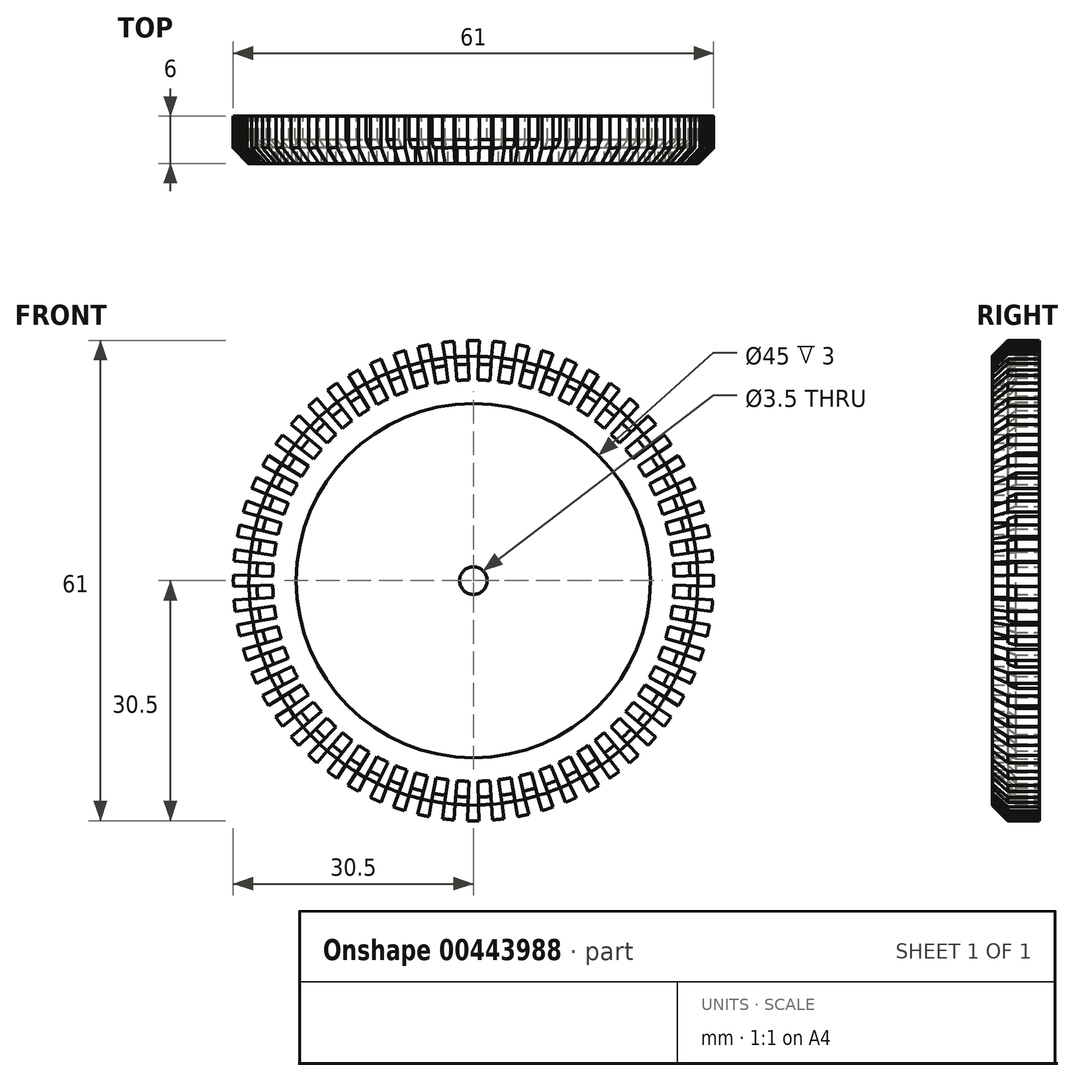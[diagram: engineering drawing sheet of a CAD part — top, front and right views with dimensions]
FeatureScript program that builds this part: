
annotation { "Feature Type Name" : "Feature", "Feature Type Description" : "" }
export const myFeature = defineFeature(function(context is Context, id is Id, definition is map)
    precondition{}
    {
        {
            var Q0;
            Q0=qCreatedBy(makeId("Front.planeOp"),FACE);
            var sketch = newSketch(context, id + "F0", { "sketchPlane" : qUnion([Q0])});
            skCircle(sketch, "E0", {"center": v(0, 0) * mm, "radius": 30.5 * mm});
            skLineSegment(sketch, "E1", {"start": v(0, 0) * mm, "end": v(-1.6, 30.46) * mm});
            skLineSegment(sketch, "E2", {"start": v(0, 0) * mm, "end": v(1.6, 30.46) * mm});
            skCircle(sketch, "E3", {"center": v(0, 0) * mm, "radius": 28.5 * mm});
            skCircle(sketch, "E4", {"center": v(0, 0) * mm, "radius": 25.5 * mm});
            skCircle(sketch, "E5", {"center": v(0, 0) * mm, "radius": 22.5 * mm});
            skLineSegment(sketch, "E6", {"start": v(-1.6, 30.46) * mm, "end": v(1.6, 30.46) * mm, "construction": true});
            skLineSegment(sketch, "E7", {"start": v(0, 0) * mm, "end": v(0, 30.5) * mm, "construction": true});
            skPoint(sketch, "E7.endSnap0", {"position": v(0, 30.46) * mm});
            skLineSegment(sketch, "E8", {"start": v(-1.33, 25.47) * mm, "end": v(1.33, 25.47) * mm, "construction": true});
            skLineSegment(sketch, "E9", {"start": v(-0.55, 25.5) * mm, "end": v(-0.75, 31.15) * mm});
            skLineSegment(sketch, "E10", {"start": v(0.55, 25.5) * mm, "end": v(0.75, 30.5) * mm});
            skCircle(sketch, "E11", {"center": v(0, 0) * mm, "radius": 1.75 * mm});
            skSolve(sketch);
        }
        {
            var Q0;
            {var subQ5=sQuery(id+"F0.wireOp",EDGE,"E5");var subQ6=sQuery(id+"F0.wireOp",EDGE,"E1");var subQ7=makeQuery(id+"F0.imprint","INTERSECT",VERTEX,{"derivedFrom":[subQ6,subQ5]});Q0=makeQuery(id+"F0.imprint","IMPRINT",FACE,{"disambiguationData":[TD([[makeQuery(id+"F0.imprint","IMPRINT",EDGE,{"disambiguationData":[TD([[subQ7,-1.0]])],"derivedFrom":subQ6}),-1.0]])]});}
            var Q1;
            {var subQ0=sQuery(id+"F0.wireOp",EDGE,"E10");var subQ1=sQuery(id+"F0.wireOp",EDGE,"E3");var subQ2=makeQuery(id+"F0.imprint","INTERSECT",VERTEX,{"derivedFrom":[subQ1,subQ0]});Q1=makeQuery(id+"F0.imprint","IMPRINT",FACE,{"disambiguationData":[TD([[makeQuery(id+"F0.imprint","IMPRINT",EDGE,{"disambiguationData":[TD([[subQ2,-1.0]])],"derivedFrom":subQ1}),1.0]])]});}
            var Q2;
            {var subQ0=sQuery(id+"F0.wireOp",EDGE,"E10");var subQ1=sQuery(id+"F0.wireOp",EDGE,"E0");var subQ2=makeQuery(id+"F0.imprint","INTERSECT",VERTEX,{"derivedFrom":[subQ1,subQ0]});Q2=makeQuery(id+"F0.imprint","IMPRINT",FACE,{"disambiguationData":[TD([[makeQuery(id+"F0.imprint","IMPRINT",EDGE,{"disambiguationData":[TD([[subQ2,-1.0]])],"derivedFrom":subQ1}),1.0]])]});}
            extrude(context, id + "F1", {"entities" : qUnion([Q0, Q1, Q2]), "depth" : 6 * mm});
        }
        {
            var Q0;
            Q0=makeQuery(id+"F1.opExtrude","SWEPT_FACE",FACE,{"disambiguationData":[OSD([sQuery(id+"F0.wireOp",EDGE,"E10")])]});
            var sketch = newSketch(context, id + "F2", { "sketchPlane" : qUnion([Q0])});
            skLineSegment(sketch, "E12.0", {"start": v(0, 25.5) * mm, "end": v(0, 30.5) * mm});
            skLineSegment(sketch, "E12.1", {"start": v(-6, 30.5) * mm, "end": v(0, 30.5) * mm});
            skLineSegment(sketch, "E12.2", {"start": v(-6, 25.5) * mm, "end": v(-6, 30.5) * mm});
            skLineSegment(sketch, "E12.3", {"start": v(-6, 25.5) * mm, "end": v(0, 25.5) * mm});
            skLineSegment(sketch, "E13", {"start": v(-6, 28.5) * mm, "end": v(0, 28.5) * mm, "construction": true});
            skLineSegment(sketch, "E14", {"start": v(-4, 25.5) * mm, "end": v(-4, 30.5) * mm, "construction": true});
            skLineSegment(sketch, "E15", {"start": v(-6, 28.5) * mm, "end": v(-4, 30.5) * mm});
            skSolve(sketch);
        }
        {
            var Q0;
            {var subQ3=sQuery(id+"F2.wireOp",EDGE,"E15");Q0=makeQuery(id+"F2.imprint","IMPRINT",FACE,{"disambiguationData":[TD([[makeQuery(id+"F2.imprint","IMPRINT",EDGE,{"derivedFrom":subQ3}),1.0]])]});}
            extrude(context, id + "F3", {"entities" : qUnion([Q0]), "operationType" : NewBodyOperationType.REMOVE, "endBound" : BoundingType.THROUGH_ALL, "oppositeDirection" : true, "depth" : 25 * mm});
        }
        {
            var Q0;
            Q0=makeQuery(id+"F1.opExtrude","SWEPT_BODY",BODY,{"disambiguationData":[OSD([sQuery(id+"F0.wireOp",EDGE,"E0"),sQuery(id+"F0.wireOp",EDGE,"E1"),sQuery(id+"F0.wireOp",EDGE,"E2"),sQuery(id+"F0.wireOp",EDGE,"E4"),sQuery(id+"F0.wireOp",EDGE,"E5"),sQuery(id+"F0.wireOp",EDGE,"E9"),sQuery(id+"F0.wireOp",EDGE,"E10")])]});
            var Q1;
            Q1=sQuery(id+"F0.wireOp",EDGE,"E5");
            circularPattern(context, id + "F4", {"operationType" : NewBodyOperationType.ADD, "entities" : qUnion([Q0]), "axis" : qUnion([Q1]), "angle" : 360 * degree, "instanceCount" : 60, "equalSpace" : true});
        }
        {
            var Q0;
            {var subQ0=sQuery(id+"F0.wireOp",EDGE,"E11");var subQ1=sQuery(id+"F0.wireOp",EDGE,"E1");var subQ2=makeQuery(id+"F0.imprint","INTERSECT",VERTEX,{"derivedFrom":[subQ1,subQ0]});Q0=makeQuery(id+"F0.imprint","IMPRINT",FACE,{"disambiguationData":[TD([[makeQuery(id+"F0.imprint","IMPRINT",EDGE,{"disambiguationData":[TD([[subQ2,-1.0]])],"derivedFrom":subQ1}),1.0]])]});}
            var Q1;
            {var subQ0=sQuery(id+"F0.wireOp",EDGE,"E11");var subQ1=sQuery(id+"F0.wireOp",EDGE,"E1");var subQ2=makeQuery(id+"F0.imprint","INTERSECT",VERTEX,{"derivedFrom":[subQ1,subQ0]});Q1=makeQuery(id+"F0.imprint","IMPRINT",FACE,{"disambiguationData":[TD([[makeQuery(id+"F0.imprint","IMPRINT",EDGE,{"disambiguationData":[TD([[subQ2,-1.0]])],"derivedFrom":subQ1}),-1.0]])]});}
            extrude(context, id + "F5", {"entities" : qUnion([Q0, Q1]), "operationType" : NewBodyOperationType.ADD, "depth" : 3 * mm});
        }
        {
            var Q0;
            {var subQ0=sQuery(id+"F0.wireOp",EDGE,"E4");var subQ1=sQuery(id+"F0.wireOp",EDGE,"E1");var subQ2=makeQuery(id+"F0.imprint","INTERSECT",VERTEX,{"derivedFrom":[subQ1,subQ0]});Q0=makeQuery(id+"F0.imprint","IMPRINT",FACE,{"disambiguationData":[TD([[makeQuery(id+"F0.imprint","IMPRINT",EDGE,{"disambiguationData":[TD([[subQ2,-1.0]])],"derivedFrom":subQ1}),1.0]])]});}
            var Q1;
            {var subQ0=sQuery(id+"F0.wireOp",EDGE,"E4");var subQ1=sQuery(id+"F0.wireOp",EDGE,"E2");var subQ2=makeQuery(id+"F0.imprint","INTERSECT",VERTEX,{"derivedFrom":[subQ1,subQ0]});Q1=makeQuery(id+"F0.imprint","IMPRINT",FACE,{"disambiguationData":[TD([[makeQuery(id+"F0.imprint","IMPRINT",EDGE,{"disambiguationData":[TD([[subQ2,-1.0]])],"derivedFrom":subQ1}),1.0]])]});}
            var Q2;
            {var subQ0=sQuery(id+"F0.wireOp",EDGE,"E4");var subQ1=sQuery(id+"F0.wireOp",EDGE,"E1");var subQ2=makeQuery(id+"F0.imprint","INTERSECT",VERTEX,{"derivedFrom":[subQ1,subQ0]});Q2=makeQuery(id+"F0.imprint","IMPRINT",FACE,{"disambiguationData":[TD([[makeQuery(id+"F0.imprint","IMPRINT",EDGE,{"disambiguationData":[TD([[subQ2,-1.0]])],"derivedFrom":subQ1}),-1.0]])]});}
            extrude(context, id + "F6", {"entities" : qUnion([Q0, Q1, Q2]), "operationType" : NewBodyOperationType.ADD, "depth" : 4 * mm});
        }
        {
            var Q0;
            {var subQ0=sQuery(id+"F0.wireOp",EDGE,"E9");var subQ1=sQuery(id+"F0.wireOp",EDGE,"E3");Q0=makeQuery(id+"F6.boolean.opBoolean","SPLIT",EDGE,{"disambiguationData":[TD([makeQuery(id+"F4.opPattern","COPY",FACE,{"derivedFrom":makeQuery(id+"F1.opExtrude","SWEPT_FACE",FACE,{"disambiguationData":[OSD([subQ0])]}),"instanceName":"56"})])],"derivedFrom":makeQuery(id+"F6.opExtrude","CAP_EDGE",EDGE,{"disambiguationData":[OSD([subQ1])],"isStart":false})});}
            var Q1;
            {var subQ0=sQuery(id+"F0.wireOp",EDGE,"E9");var subQ2=sQuery(id+"F0.wireOp",EDGE,"E3");Q1=makeQuery(id+"F6.boolean.opBoolean","SPLIT",EDGE,{"disambiguationData":[TD([makeQuery(id+"F4.opPattern","COPY",FACE,{"derivedFrom":makeQuery(id+"F1.opExtrude","SWEPT_FACE",FACE,{"disambiguationData":[OSD([subQ0])]}),"instanceName":"55"})])],"derivedFrom":makeQuery(id+"F6.opExtrude","CAP_EDGE",EDGE,{"disambiguationData":[OSD([subQ2])],"isStart":false})});}
            var Q2;
            {var subQ0=sQuery(id+"F0.wireOp",EDGE,"E9");var subQ2=sQuery(id+"F0.wireOp",EDGE,"E3");Q2=makeQuery(id+"F6.boolean.opBoolean","SPLIT",EDGE,{"disambiguationData":[TD([makeQuery(id+"F4.opPattern","COPY",FACE,{"derivedFrom":makeQuery(id+"F1.opExtrude","SWEPT_FACE",FACE,{"disambiguationData":[OSD([subQ0])]}),"instanceName":"54"})])],"derivedFrom":makeQuery(id+"F6.opExtrude","CAP_EDGE",EDGE,{"disambiguationData":[OSD([subQ2])],"isStart":false})});}
            var Q3;
            {var subQ0=sQuery(id+"F0.wireOp",EDGE,"E9");var subQ2=sQuery(id+"F0.wireOp",EDGE,"E3");Q3=makeQuery(id+"F6.boolean.opBoolean","SPLIT",EDGE,{"disambiguationData":[TD([makeQuery(id+"F4.opPattern","COPY",FACE,{"derivedFrom":makeQuery(id+"F1.opExtrude","SWEPT_FACE",FACE,{"disambiguationData":[OSD([subQ0])]}),"instanceName":"57"})])],"derivedFrom":makeQuery(id+"F6.opExtrude","CAP_EDGE",EDGE,{"disambiguationData":[OSD([subQ2])],"isStart":false})});}
            var Q4;
            {var subQ0=sQuery(id+"F0.wireOp",EDGE,"E9");var subQ2=sQuery(id+"F0.wireOp",EDGE,"E3");Q4=makeQuery(id+"F6.boolean.opBoolean","SPLIT",EDGE,{"disambiguationData":[TD([makeQuery(id+"F4.opPattern","COPY",FACE,{"derivedFrom":makeQuery(id+"F1.opExtrude","SWEPT_FACE",FACE,{"disambiguationData":[OSD([subQ0])]}),"instanceName":"58"})])],"derivedFrom":makeQuery(id+"F6.opExtrude","CAP_EDGE",EDGE,{"disambiguationData":[OSD([subQ2])],"isStart":false})});}
            var Q5;
            {var subQ0=sQuery(id+"F0.wireOp",EDGE,"E10");var subQ1=sQuery(id+"F0.wireOp",EDGE,"E3");Q5=makeQuery(id+"F6.boolean.opBoolean","SPLIT",EDGE,{"disambiguationData":[TD([makeQuery(id+"F1.opExtrude","SWEPT_FACE",FACE,{"disambiguationData":[OSD([subQ0])]})])],"derivedFrom":makeQuery(id+"F6.opExtrude","CAP_EDGE",EDGE,{"disambiguationData":[OSD([subQ1])],"isStart":false})});}
            var Q6;
            {var subQ0=sQuery(id+"F0.wireOp",EDGE,"E9");var subQ2=sQuery(id+"F0.wireOp",EDGE,"E3");Q6=makeQuery(id+"F6.boolean.opBoolean","SPLIT",EDGE,{"disambiguationData":[TD([makeQuery(id+"F1.opExtrude","SWEPT_FACE",FACE,{"disambiguationData":[OSD([subQ0])]})])],"derivedFrom":makeQuery(id+"F6.opExtrude","CAP_EDGE",EDGE,{"disambiguationData":[OSD([subQ2])],"isStart":false})});}
            var Q7;
            {var subQ0=sQuery(id+"F0.wireOp",EDGE,"E9");var subQ1=sQuery(id+"F0.wireOp",EDGE,"E3");Q7=makeQuery(id+"F6.boolean.opBoolean","SPLIT",EDGE,{"disambiguationData":[TD([makeQuery(id+"F4.opPattern","COPY",FACE,{"derivedFrom":makeQuery(id+"F1.opExtrude","SWEPT_FACE",FACE,{"disambiguationData":[OSD([subQ0])]}),"instanceName":"1"})])],"derivedFrom":makeQuery(id+"F6.opExtrude","CAP_EDGE",EDGE,{"disambiguationData":[OSD([subQ1])],"isStart":false})});}
            var Q8;
            {var subQ0=sQuery(id+"F0.wireOp",EDGE,"E9");var subQ2=sQuery(id+"F0.wireOp",EDGE,"E3");Q8=makeQuery(id+"F6.boolean.opBoolean","SPLIT",EDGE,{"disambiguationData":[TD([makeQuery(id+"F4.opPattern","COPY",FACE,{"derivedFrom":makeQuery(id+"F1.opExtrude","SWEPT_FACE",FACE,{"disambiguationData":[OSD([subQ0])]}),"instanceName":"2"})])],"derivedFrom":makeQuery(id+"F6.opExtrude","CAP_EDGE",EDGE,{"disambiguationData":[OSD([subQ2])],"isStart":false})});}
            var Q9;
            {var subQ0=sQuery(id+"F0.wireOp",EDGE,"E9");var subQ2=sQuery(id+"F0.wireOp",EDGE,"E3");Q9=makeQuery(id+"F6.boolean.opBoolean","SPLIT",EDGE,{"disambiguationData":[TD([makeQuery(id+"F4.opPattern","COPY",FACE,{"derivedFrom":makeQuery(id+"F1.opExtrude","SWEPT_FACE",FACE,{"disambiguationData":[OSD([subQ0])]}),"instanceName":"53"})])],"derivedFrom":makeQuery(id+"F6.opExtrude","CAP_EDGE",EDGE,{"disambiguationData":[OSD([subQ2])],"isStart":false})});}
            var Q10;
            {var subQ0=sQuery(id+"F0.wireOp",EDGE,"E9");var subQ2=sQuery(id+"F0.wireOp",EDGE,"E3");Q10=makeQuery(id+"F6.boolean.opBoolean","SPLIT",EDGE,{"disambiguationData":[TD([makeQuery(id+"F4.opPattern","COPY",FACE,{"derivedFrom":makeQuery(id+"F1.opExtrude","SWEPT_FACE",FACE,{"disambiguationData":[OSD([subQ0])]}),"instanceName":"52"})])],"derivedFrom":makeQuery(id+"F6.opExtrude","CAP_EDGE",EDGE,{"disambiguationData":[OSD([subQ2])],"isStart":false})});}
            var Q11;
            {var subQ0=sQuery(id+"F0.wireOp",EDGE,"E9");var subQ1=sQuery(id+"F0.wireOp",EDGE,"E3");Q11=makeQuery(id+"F6.boolean.opBoolean","SPLIT",EDGE,{"disambiguationData":[TD([makeQuery(id+"F4.opPattern","COPY",FACE,{"derivedFrom":makeQuery(id+"F1.opExtrude","SWEPT_FACE",FACE,{"disambiguationData":[OSD([subQ0])]}),"instanceName":"51"})])],"derivedFrom":makeQuery(id+"F6.opExtrude","CAP_EDGE",EDGE,{"disambiguationData":[OSD([subQ1])],"isStart":false})});}
            var Q12;
            {var subQ0=sQuery(id+"F0.wireOp",EDGE,"E9");var subQ2=sQuery(id+"F0.wireOp",EDGE,"E3");Q12=makeQuery(id+"F6.boolean.opBoolean","SPLIT",EDGE,{"disambiguationData":[TD([makeQuery(id+"F4.opPattern","COPY",FACE,{"derivedFrom":makeQuery(id+"F1.opExtrude","SWEPT_FACE",FACE,{"disambiguationData":[OSD([subQ0])]}),"instanceName":"50"})])],"derivedFrom":makeQuery(id+"F6.opExtrude","CAP_EDGE",EDGE,{"disambiguationData":[OSD([subQ2])],"isStart":false})});}
            var Q13;
            {var subQ0=sQuery(id+"F0.wireOp",EDGE,"E9");var subQ2=sQuery(id+"F0.wireOp",EDGE,"E3");Q13=makeQuery(id+"F6.boolean.opBoolean","SPLIT",EDGE,{"disambiguationData":[TD([makeQuery(id+"F4.opPattern","COPY",FACE,{"derivedFrom":makeQuery(id+"F1.opExtrude","SWEPT_FACE",FACE,{"disambiguationData":[OSD([subQ0])]}),"instanceName":"49"})])],"derivedFrom":makeQuery(id+"F6.opExtrude","CAP_EDGE",EDGE,{"disambiguationData":[OSD([subQ2])],"isStart":false})});}
            var Q14;
            {var subQ0=sQuery(id+"F0.wireOp",EDGE,"E9");var subQ2=sQuery(id+"F0.wireOp",EDGE,"E3");Q14=makeQuery(id+"F6.boolean.opBoolean","SPLIT",EDGE,{"disambiguationData":[TD([makeQuery(id+"F4.opPattern","COPY",FACE,{"derivedFrom":makeQuery(id+"F1.opExtrude","SWEPT_FACE",FACE,{"disambiguationData":[OSD([subQ0])]}),"instanceName":"48"})])],"derivedFrom":makeQuery(id+"F6.opExtrude","CAP_EDGE",EDGE,{"disambiguationData":[OSD([subQ2])],"isStart":false})});}
            var Q15;
            {var subQ0=sQuery(id+"F0.wireOp",EDGE,"E9");var subQ2=sQuery(id+"F0.wireOp",EDGE,"E3");Q15=makeQuery(id+"F6.boolean.opBoolean","SPLIT",EDGE,{"disambiguationData":[TD([makeQuery(id+"F4.opPattern","COPY",FACE,{"derivedFrom":makeQuery(id+"F1.opExtrude","SWEPT_FACE",FACE,{"disambiguationData":[OSD([subQ0])]}),"instanceName":"47"})])],"derivedFrom":makeQuery(id+"F6.opExtrude","CAP_EDGE",EDGE,{"disambiguationData":[OSD([subQ2])],"isStart":false})});}
            var Q16;
            {var subQ0=sQuery(id+"F0.wireOp",EDGE,"E9");var subQ1=sQuery(id+"F0.wireOp",EDGE,"E3");Q16=makeQuery(id+"F6.boolean.opBoolean","SPLIT",EDGE,{"disambiguationData":[TD([makeQuery(id+"F4.opPattern","COPY",FACE,{"derivedFrom":makeQuery(id+"F1.opExtrude","SWEPT_FACE",FACE,{"disambiguationData":[OSD([subQ0])]}),"instanceName":"46"})])],"derivedFrom":makeQuery(id+"F6.opExtrude","CAP_EDGE",EDGE,{"disambiguationData":[OSD([subQ1])],"isStart":false})});}
            var Q17;
            {var subQ0=sQuery(id+"F0.wireOp",EDGE,"E9");var subQ2=sQuery(id+"F0.wireOp",EDGE,"E3");Q17=makeQuery(id+"F6.boolean.opBoolean","SPLIT",EDGE,{"disambiguationData":[TD([makeQuery(id+"F4.opPattern","COPY",FACE,{"derivedFrom":makeQuery(id+"F1.opExtrude","SWEPT_FACE",FACE,{"disambiguationData":[OSD([subQ0])]}),"instanceName":"45"})])],"derivedFrom":makeQuery(id+"F6.opExtrude","CAP_EDGE",EDGE,{"disambiguationData":[OSD([subQ2])],"isStart":false})});}
            var Q18;
            {var subQ0=sQuery(id+"F0.wireOp",EDGE,"E9");var subQ2=sQuery(id+"F0.wireOp",EDGE,"E3");Q18=makeQuery(id+"F6.boolean.opBoolean","SPLIT",EDGE,{"disambiguationData":[TD([makeQuery(id+"F4.opPattern","COPY",FACE,{"derivedFrom":makeQuery(id+"F1.opExtrude","SWEPT_FACE",FACE,{"disambiguationData":[OSD([subQ0])]}),"instanceName":"44"})])],"derivedFrom":makeQuery(id+"F6.opExtrude","CAP_EDGE",EDGE,{"disambiguationData":[OSD([subQ2])],"isStart":false})});}
            var Q19;
            {var subQ0=sQuery(id+"F0.wireOp",EDGE,"E9");var subQ2=sQuery(id+"F0.wireOp",EDGE,"E3");Q19=makeQuery(id+"F6.boolean.opBoolean","SPLIT",EDGE,{"disambiguationData":[TD([makeQuery(id+"F4.opPattern","COPY",FACE,{"derivedFrom":makeQuery(id+"F1.opExtrude","SWEPT_FACE",FACE,{"disambiguationData":[OSD([subQ0])]}),"instanceName":"43"})])],"derivedFrom":makeQuery(id+"F6.opExtrude","CAP_EDGE",EDGE,{"disambiguationData":[OSD([subQ2])],"isStart":false})});}
            var Q20;
            {var subQ0=sQuery(id+"F0.wireOp",EDGE,"E9");var subQ2=sQuery(id+"F0.wireOp",EDGE,"E3");Q20=makeQuery(id+"F6.boolean.opBoolean","SPLIT",EDGE,{"disambiguationData":[TD([makeQuery(id+"F4.opPattern","COPY",FACE,{"derivedFrom":makeQuery(id+"F1.opExtrude","SWEPT_FACE",FACE,{"disambiguationData":[OSD([subQ0])]}),"instanceName":"42"})])],"derivedFrom":makeQuery(id+"F6.opExtrude","CAP_EDGE",EDGE,{"disambiguationData":[OSD([subQ2])],"isStart":false})});}
            var Q21;
            {var subQ0=sQuery(id+"F0.wireOp",EDGE,"E9");var subQ1=sQuery(id+"F0.wireOp",EDGE,"E3");Q21=makeQuery(id+"F6.boolean.opBoolean","SPLIT",EDGE,{"disambiguationData":[TD([makeQuery(id+"F4.opPattern","COPY",FACE,{"derivedFrom":makeQuery(id+"F1.opExtrude","SWEPT_FACE",FACE,{"disambiguationData":[OSD([subQ0])]}),"instanceName":"41"})])],"derivedFrom":makeQuery(id+"F6.opExtrude","CAP_EDGE",EDGE,{"disambiguationData":[OSD([subQ1])],"isStart":false})});}
            var Q22;
            {var subQ0=sQuery(id+"F0.wireOp",EDGE,"E9");var subQ2=sQuery(id+"F0.wireOp",EDGE,"E3");Q22=makeQuery(id+"F6.boolean.opBoolean","SPLIT",EDGE,{"disambiguationData":[TD([makeQuery(id+"F4.opPattern","COPY",FACE,{"derivedFrom":makeQuery(id+"F1.opExtrude","SWEPT_FACE",FACE,{"disambiguationData":[OSD([subQ0])]}),"instanceName":"40"})])],"derivedFrom":makeQuery(id+"F6.opExtrude","CAP_EDGE",EDGE,{"disambiguationData":[OSD([subQ2])],"isStart":false})});}
            var Q23;
            {var subQ0=sQuery(id+"F0.wireOp",EDGE,"E9");var subQ2=sQuery(id+"F0.wireOp",EDGE,"E3");Q23=makeQuery(id+"F6.boolean.opBoolean","SPLIT",EDGE,{"disambiguationData":[TD([makeQuery(id+"F4.opPattern","COPY",FACE,{"derivedFrom":makeQuery(id+"F1.opExtrude","SWEPT_FACE",FACE,{"disambiguationData":[OSD([subQ0])]}),"instanceName":"39"})])],"derivedFrom":makeQuery(id+"F6.opExtrude","CAP_EDGE",EDGE,{"disambiguationData":[OSD([subQ2])],"isStart":false})});}
            var Q24;
            {var subQ0=sQuery(id+"F0.wireOp",EDGE,"E9");var subQ2=sQuery(id+"F0.wireOp",EDGE,"E3");Q24=makeQuery(id+"F6.boolean.opBoolean","SPLIT",EDGE,{"disambiguationData":[TD([makeQuery(id+"F4.opPattern","COPY",FACE,{"derivedFrom":makeQuery(id+"F1.opExtrude","SWEPT_FACE",FACE,{"disambiguationData":[OSD([subQ0])]}),"instanceName":"38"})])],"derivedFrom":makeQuery(id+"F6.opExtrude","CAP_EDGE",EDGE,{"disambiguationData":[OSD([subQ2])],"isStart":false})});}
            var Q25;
            {var subQ0=sQuery(id+"F0.wireOp",EDGE,"E9");var subQ2=sQuery(id+"F0.wireOp",EDGE,"E3");Q25=makeQuery(id+"F6.boolean.opBoolean","SPLIT",EDGE,{"disambiguationData":[TD([makeQuery(id+"F4.opPattern","COPY",FACE,{"derivedFrom":makeQuery(id+"F1.opExtrude","SWEPT_FACE",FACE,{"disambiguationData":[OSD([subQ0])]}),"instanceName":"37"})])],"derivedFrom":makeQuery(id+"F6.opExtrude","CAP_EDGE",EDGE,{"disambiguationData":[OSD([subQ2])],"isStart":false})});}
            var Q26;
            {var subQ0=sQuery(id+"F0.wireOp",EDGE,"E9");var subQ1=sQuery(id+"F0.wireOp",EDGE,"E3");Q26=makeQuery(id+"F6.boolean.opBoolean","SPLIT",EDGE,{"disambiguationData":[TD([makeQuery(id+"F4.opPattern","COPY",FACE,{"derivedFrom":makeQuery(id+"F1.opExtrude","SWEPT_FACE",FACE,{"disambiguationData":[OSD([subQ0])]}),"instanceName":"36"})])],"derivedFrom":makeQuery(id+"F6.opExtrude","CAP_EDGE",EDGE,{"disambiguationData":[OSD([subQ1])],"isStart":false})});}
            var Q27;
            {var subQ0=sQuery(id+"F0.wireOp",EDGE,"E9");var subQ2=sQuery(id+"F0.wireOp",EDGE,"E3");Q27=makeQuery(id+"F6.boolean.opBoolean","SPLIT",EDGE,{"disambiguationData":[TD([makeQuery(id+"F4.opPattern","COPY",FACE,{"derivedFrom":makeQuery(id+"F1.opExtrude","SWEPT_FACE",FACE,{"disambiguationData":[OSD([subQ0])]}),"instanceName":"35"})])],"derivedFrom":makeQuery(id+"F6.opExtrude","CAP_EDGE",EDGE,{"disambiguationData":[OSD([subQ2])],"isStart":false})});}
            var Q28;
            {var subQ0=sQuery(id+"F0.wireOp",EDGE,"E9");var subQ2=sQuery(id+"F0.wireOp",EDGE,"E3");Q28=makeQuery(id+"F6.boolean.opBoolean","SPLIT",EDGE,{"disambiguationData":[TD([makeQuery(id+"F4.opPattern","COPY",FACE,{"derivedFrom":makeQuery(id+"F1.opExtrude","SWEPT_FACE",FACE,{"disambiguationData":[OSD([subQ0])]}),"instanceName":"34"})])],"derivedFrom":makeQuery(id+"F6.opExtrude","CAP_EDGE",EDGE,{"disambiguationData":[OSD([subQ2])],"isStart":false})});}
            var Q29;
            {var subQ0=sQuery(id+"F0.wireOp",EDGE,"E9");var subQ2=sQuery(id+"F0.wireOp",EDGE,"E3");Q29=makeQuery(id+"F6.boolean.opBoolean","SPLIT",EDGE,{"disambiguationData":[TD([makeQuery(id+"F4.opPattern","COPY",FACE,{"derivedFrom":makeQuery(id+"F1.opExtrude","SWEPT_FACE",FACE,{"disambiguationData":[OSD([subQ0])]}),"instanceName":"33"})])],"derivedFrom":makeQuery(id+"F6.opExtrude","CAP_EDGE",EDGE,{"disambiguationData":[OSD([subQ2])],"isStart":false})});}
            var Q30;
            {var subQ0=sQuery(id+"F0.wireOp",EDGE,"E9");var subQ2=sQuery(id+"F0.wireOp",EDGE,"E3");Q30=makeQuery(id+"F6.boolean.opBoolean","SPLIT",EDGE,{"disambiguationData":[TD([makeQuery(id+"F4.opPattern","COPY",FACE,{"derivedFrom":makeQuery(id+"F1.opExtrude","SWEPT_FACE",FACE,{"disambiguationData":[OSD([subQ0])]}),"instanceName":"32"})])],"derivedFrom":makeQuery(id+"F6.opExtrude","CAP_EDGE",EDGE,{"disambiguationData":[OSD([subQ2])],"isStart":false})});}
            var Q31;
            {var subQ0=sQuery(id+"F0.wireOp",EDGE,"E9");var subQ1=sQuery(id+"F0.wireOp",EDGE,"E3");Q31=makeQuery(id+"F6.boolean.opBoolean","SPLIT",EDGE,{"disambiguationData":[TD([makeQuery(id+"F4.opPattern","COPY",FACE,{"derivedFrom":makeQuery(id+"F1.opExtrude","SWEPT_FACE",FACE,{"disambiguationData":[OSD([subQ0])]}),"instanceName":"31"})])],"derivedFrom":makeQuery(id+"F6.opExtrude","CAP_EDGE",EDGE,{"disambiguationData":[OSD([subQ1])],"isStart":false})});}
            var Q32;
            {var subQ0=sQuery(id+"F0.wireOp",EDGE,"E9");var subQ2=sQuery(id+"F0.wireOp",EDGE,"E3");Q32=makeQuery(id+"F6.boolean.opBoolean","SPLIT",EDGE,{"disambiguationData":[TD([makeQuery(id+"F4.opPattern","COPY",FACE,{"derivedFrom":makeQuery(id+"F1.opExtrude","SWEPT_FACE",FACE,{"disambiguationData":[OSD([subQ0])]}),"instanceName":"30"})])],"derivedFrom":makeQuery(id+"F6.opExtrude","CAP_EDGE",EDGE,{"disambiguationData":[OSD([subQ2])],"isStart":false})});}
            var Q33;
            {var subQ0=sQuery(id+"F0.wireOp",EDGE,"E9");var subQ2=sQuery(id+"F0.wireOp",EDGE,"E3");Q33=makeQuery(id+"F6.boolean.opBoolean","SPLIT",EDGE,{"disambiguationData":[TD([makeQuery(id+"F4.opPattern","COPY",FACE,{"derivedFrom":makeQuery(id+"F1.opExtrude","SWEPT_FACE",FACE,{"disambiguationData":[OSD([subQ0])]}),"instanceName":"29"})])],"derivedFrom":makeQuery(id+"F6.opExtrude","CAP_EDGE",EDGE,{"disambiguationData":[OSD([subQ2])],"isStart":false})});}
            var Q34;
            {var subQ0=sQuery(id+"F0.wireOp",EDGE,"E9");var subQ2=sQuery(id+"F0.wireOp",EDGE,"E3");Q34=makeQuery(id+"F6.boolean.opBoolean","SPLIT",EDGE,{"disambiguationData":[TD([makeQuery(id+"F4.opPattern","COPY",FACE,{"derivedFrom":makeQuery(id+"F1.opExtrude","SWEPT_FACE",FACE,{"disambiguationData":[OSD([subQ0])]}),"instanceName":"28"})])],"derivedFrom":makeQuery(id+"F6.opExtrude","CAP_EDGE",EDGE,{"disambiguationData":[OSD([subQ2])],"isStart":false})});}
            var Q35;
            {var subQ0=sQuery(id+"F0.wireOp",EDGE,"E9");var subQ2=sQuery(id+"F0.wireOp",EDGE,"E3");Q35=makeQuery(id+"F6.boolean.opBoolean","SPLIT",EDGE,{"disambiguationData":[TD([makeQuery(id+"F4.opPattern","COPY",FACE,{"derivedFrom":makeQuery(id+"F1.opExtrude","SWEPT_FACE",FACE,{"disambiguationData":[OSD([subQ0])]}),"instanceName":"27"})])],"derivedFrom":makeQuery(id+"F6.opExtrude","CAP_EDGE",EDGE,{"disambiguationData":[OSD([subQ2])],"isStart":false})});}
            var Q36;
            {var subQ0=sQuery(id+"F0.wireOp",EDGE,"E9");var subQ1=sQuery(id+"F0.wireOp",EDGE,"E3");Q36=makeQuery(id+"F6.boolean.opBoolean","SPLIT",EDGE,{"disambiguationData":[TD([makeQuery(id+"F4.opPattern","COPY",FACE,{"derivedFrom":makeQuery(id+"F1.opExtrude","SWEPT_FACE",FACE,{"disambiguationData":[OSD([subQ0])]}),"instanceName":"26"})])],"derivedFrom":makeQuery(id+"F6.opExtrude","CAP_EDGE",EDGE,{"disambiguationData":[OSD([subQ1])],"isStart":false})});}
            var Q37;
            {var subQ0=sQuery(id+"F0.wireOp",EDGE,"E9");var subQ2=sQuery(id+"F0.wireOp",EDGE,"E3");Q37=makeQuery(id+"F6.boolean.opBoolean","SPLIT",EDGE,{"disambiguationData":[TD([makeQuery(id+"F4.opPattern","COPY",FACE,{"derivedFrom":makeQuery(id+"F1.opExtrude","SWEPT_FACE",FACE,{"disambiguationData":[OSD([subQ0])]}),"instanceName":"25"})])],"derivedFrom":makeQuery(id+"F6.opExtrude","CAP_EDGE",EDGE,{"disambiguationData":[OSD([subQ2])],"isStart":false})});}
            var Q38;
            {var subQ0=sQuery(id+"F0.wireOp",EDGE,"E9");var subQ2=sQuery(id+"F0.wireOp",EDGE,"E3");Q38=makeQuery(id+"F6.boolean.opBoolean","SPLIT",EDGE,{"disambiguationData":[TD([makeQuery(id+"F4.opPattern","COPY",FACE,{"derivedFrom":makeQuery(id+"F1.opExtrude","SWEPT_FACE",FACE,{"disambiguationData":[OSD([subQ0])]}),"instanceName":"24"})])],"derivedFrom":makeQuery(id+"F6.opExtrude","CAP_EDGE",EDGE,{"disambiguationData":[OSD([subQ2])],"isStart":false})});}
            var Q39;
            {var subQ0=sQuery(id+"F0.wireOp",EDGE,"E9");var subQ2=sQuery(id+"F0.wireOp",EDGE,"E3");Q39=makeQuery(id+"F6.boolean.opBoolean","SPLIT",EDGE,{"disambiguationData":[TD([makeQuery(id+"F4.opPattern","COPY",FACE,{"derivedFrom":makeQuery(id+"F1.opExtrude","SWEPT_FACE",FACE,{"disambiguationData":[OSD([subQ0])]}),"instanceName":"23"})])],"derivedFrom":makeQuery(id+"F6.opExtrude","CAP_EDGE",EDGE,{"disambiguationData":[OSD([subQ2])],"isStart":false})});}
            var Q40;
            {var subQ0=sQuery(id+"F0.wireOp",EDGE,"E9");var subQ2=sQuery(id+"F0.wireOp",EDGE,"E3");Q40=makeQuery(id+"F6.boolean.opBoolean","SPLIT",EDGE,{"disambiguationData":[TD([makeQuery(id+"F4.opPattern","COPY",FACE,{"derivedFrom":makeQuery(id+"F1.opExtrude","SWEPT_FACE",FACE,{"disambiguationData":[OSD([subQ0])]}),"instanceName":"22"})])],"derivedFrom":makeQuery(id+"F6.opExtrude","CAP_EDGE",EDGE,{"disambiguationData":[OSD([subQ2])],"isStart":false})});}
            var Q41;
            {var subQ0=sQuery(id+"F0.wireOp",EDGE,"E9");var subQ1=sQuery(id+"F0.wireOp",EDGE,"E3");Q41=makeQuery(id+"F6.boolean.opBoolean","SPLIT",EDGE,{"disambiguationData":[TD([makeQuery(id+"F4.opPattern","COPY",FACE,{"derivedFrom":makeQuery(id+"F1.opExtrude","SWEPT_FACE",FACE,{"disambiguationData":[OSD([subQ0])]}),"instanceName":"21"})])],"derivedFrom":makeQuery(id+"F6.opExtrude","CAP_EDGE",EDGE,{"disambiguationData":[OSD([subQ1])],"isStart":false})});}
            var Q42;
            {var subQ0=sQuery(id+"F0.wireOp",EDGE,"E9");var subQ2=sQuery(id+"F0.wireOp",EDGE,"E3");Q42=makeQuery(id+"F6.boolean.opBoolean","SPLIT",EDGE,{"disambiguationData":[TD([makeQuery(id+"F4.opPattern","COPY",FACE,{"derivedFrom":makeQuery(id+"F1.opExtrude","SWEPT_FACE",FACE,{"disambiguationData":[OSD([subQ0])]}),"instanceName":"19"})])],"derivedFrom":makeQuery(id+"F6.opExtrude","CAP_EDGE",EDGE,{"disambiguationData":[OSD([subQ2])],"isStart":false})});}
            var Q43;
            {var subQ0=sQuery(id+"F0.wireOp",EDGE,"E9");var subQ2=sQuery(id+"F0.wireOp",EDGE,"E3");Q43=makeQuery(id+"F6.boolean.opBoolean","SPLIT",EDGE,{"disambiguationData":[TD([makeQuery(id+"F4.opPattern","COPY",FACE,{"derivedFrom":makeQuery(id+"F1.opExtrude","SWEPT_FACE",FACE,{"disambiguationData":[OSD([subQ0])]}),"instanceName":"20"})])],"derivedFrom":makeQuery(id+"F6.opExtrude","CAP_EDGE",EDGE,{"disambiguationData":[OSD([subQ2])],"isStart":false})});}
            var Q44;
            {var subQ0=sQuery(id+"F0.wireOp",EDGE,"E9");var subQ2=sQuery(id+"F0.wireOp",EDGE,"E3");Q44=makeQuery(id+"F6.boolean.opBoolean","SPLIT",EDGE,{"disambiguationData":[TD([makeQuery(id+"F4.opPattern","COPY",FACE,{"derivedFrom":makeQuery(id+"F1.opExtrude","SWEPT_FACE",FACE,{"disambiguationData":[OSD([subQ0])]}),"instanceName":"18"})])],"derivedFrom":makeQuery(id+"F6.opExtrude","CAP_EDGE",EDGE,{"disambiguationData":[OSD([subQ2])],"isStart":false})});}
            var Q45;
            {var subQ0=sQuery(id+"F0.wireOp",EDGE,"E9");var subQ2=sQuery(id+"F0.wireOp",EDGE,"E3");Q45=makeQuery(id+"F6.boolean.opBoolean","SPLIT",EDGE,{"disambiguationData":[TD([makeQuery(id+"F4.opPattern","COPY",FACE,{"derivedFrom":makeQuery(id+"F1.opExtrude","SWEPT_FACE",FACE,{"disambiguationData":[OSD([subQ0])]}),"instanceName":"17"})])],"derivedFrom":makeQuery(id+"F6.opExtrude","CAP_EDGE",EDGE,{"disambiguationData":[OSD([subQ2])],"isStart":false})});}
            var Q46;
            {var subQ0=sQuery(id+"F0.wireOp",EDGE,"E9");var subQ1=sQuery(id+"F0.wireOp",EDGE,"E3");Q46=makeQuery(id+"F6.boolean.opBoolean","SPLIT",EDGE,{"disambiguationData":[TD([makeQuery(id+"F4.opPattern","COPY",FACE,{"derivedFrom":makeQuery(id+"F1.opExtrude","SWEPT_FACE",FACE,{"disambiguationData":[OSD([subQ0])]}),"instanceName":"16"})])],"derivedFrom":makeQuery(id+"F6.opExtrude","CAP_EDGE",EDGE,{"disambiguationData":[OSD([subQ1])],"isStart":false})});}
            var Q47;
            {var subQ0=sQuery(id+"F0.wireOp",EDGE,"E9");var subQ2=sQuery(id+"F0.wireOp",EDGE,"E3");Q47=makeQuery(id+"F6.boolean.opBoolean","SPLIT",EDGE,{"disambiguationData":[TD([makeQuery(id+"F4.opPattern","COPY",FACE,{"derivedFrom":makeQuery(id+"F1.opExtrude","SWEPT_FACE",FACE,{"disambiguationData":[OSD([subQ0])]}),"instanceName":"15"})])],"derivedFrom":makeQuery(id+"F6.opExtrude","CAP_EDGE",EDGE,{"disambiguationData":[OSD([subQ2])],"isStart":false})});}
            var Q48;
            {var subQ0=sQuery(id+"F0.wireOp",EDGE,"E9");var subQ2=sQuery(id+"F0.wireOp",EDGE,"E3");Q48=makeQuery(id+"F6.boolean.opBoolean","SPLIT",EDGE,{"disambiguationData":[TD([makeQuery(id+"F4.opPattern","COPY",FACE,{"derivedFrom":makeQuery(id+"F1.opExtrude","SWEPT_FACE",FACE,{"disambiguationData":[OSD([subQ0])]}),"instanceName":"14"})])],"derivedFrom":makeQuery(id+"F6.opExtrude","CAP_EDGE",EDGE,{"disambiguationData":[OSD([subQ2])],"isStart":false})});}
            var Q49;
            {var subQ0=sQuery(id+"F0.wireOp",EDGE,"E9");var subQ2=sQuery(id+"F0.wireOp",EDGE,"E3");Q49=makeQuery(id+"F6.boolean.opBoolean","SPLIT",EDGE,{"disambiguationData":[TD([makeQuery(id+"F4.opPattern","COPY",FACE,{"derivedFrom":makeQuery(id+"F1.opExtrude","SWEPT_FACE",FACE,{"disambiguationData":[OSD([subQ0])]}),"instanceName":"13"})])],"derivedFrom":makeQuery(id+"F6.opExtrude","CAP_EDGE",EDGE,{"disambiguationData":[OSD([subQ2])],"isStart":false})});}
            var Q50;
            {var subQ0=sQuery(id+"F0.wireOp",EDGE,"E9");var subQ2=sQuery(id+"F0.wireOp",EDGE,"E3");Q50=makeQuery(id+"F6.boolean.opBoolean","SPLIT",EDGE,{"disambiguationData":[TD([makeQuery(id+"F4.opPattern","COPY",FACE,{"derivedFrom":makeQuery(id+"F1.opExtrude","SWEPT_FACE",FACE,{"disambiguationData":[OSD([subQ0])]}),"instanceName":"12"})])],"derivedFrom":makeQuery(id+"F6.opExtrude","CAP_EDGE",EDGE,{"disambiguationData":[OSD([subQ2])],"isStart":false})});}
            var Q51;
            {var subQ0=sQuery(id+"F0.wireOp",EDGE,"E9");var subQ1=sQuery(id+"F0.wireOp",EDGE,"E3");Q51=makeQuery(id+"F6.boolean.opBoolean","SPLIT",EDGE,{"disambiguationData":[TD([makeQuery(id+"F4.opPattern","COPY",FACE,{"derivedFrom":makeQuery(id+"F1.opExtrude","SWEPT_FACE",FACE,{"disambiguationData":[OSD([subQ0])]}),"instanceName":"11"})])],"derivedFrom":makeQuery(id+"F6.opExtrude","CAP_EDGE",EDGE,{"disambiguationData":[OSD([subQ1])],"isStart":false})});}
            var Q52;
            {var subQ0=sQuery(id+"F0.wireOp",EDGE,"E9");var subQ2=sQuery(id+"F0.wireOp",EDGE,"E3");Q52=makeQuery(id+"F6.boolean.opBoolean","SPLIT",EDGE,{"disambiguationData":[TD([makeQuery(id+"F4.opPattern","COPY",FACE,{"derivedFrom":makeQuery(id+"F1.opExtrude","SWEPT_FACE",FACE,{"disambiguationData":[OSD([subQ0])]}),"instanceName":"10"})])],"derivedFrom":makeQuery(id+"F6.opExtrude","CAP_EDGE",EDGE,{"disambiguationData":[OSD([subQ2])],"isStart":false})});}
            var Q53;
            {var subQ0=sQuery(id+"F0.wireOp",EDGE,"E9");var subQ2=sQuery(id+"F0.wireOp",EDGE,"E3");Q53=makeQuery(id+"F6.boolean.opBoolean","SPLIT",EDGE,{"disambiguationData":[TD([makeQuery(id+"F4.opPattern","COPY",FACE,{"derivedFrom":makeQuery(id+"F1.opExtrude","SWEPT_FACE",FACE,{"disambiguationData":[OSD([subQ0])]}),"instanceName":"9"})])],"derivedFrom":makeQuery(id+"F6.opExtrude","CAP_EDGE",EDGE,{"disambiguationData":[OSD([subQ2])],"isStart":false})});}
            var Q54;
            {var subQ0=sQuery(id+"F0.wireOp",EDGE,"E9");var subQ2=sQuery(id+"F0.wireOp",EDGE,"E3");Q54=makeQuery(id+"F6.boolean.opBoolean","SPLIT",EDGE,{"disambiguationData":[TD([makeQuery(id+"F4.opPattern","COPY",FACE,{"derivedFrom":makeQuery(id+"F1.opExtrude","SWEPT_FACE",FACE,{"disambiguationData":[OSD([subQ0])]}),"instanceName":"8"})])],"derivedFrom":makeQuery(id+"F6.opExtrude","CAP_EDGE",EDGE,{"disambiguationData":[OSD([subQ2])],"isStart":false})});}
            var Q55;
            {var subQ0=sQuery(id+"F0.wireOp",EDGE,"E9");var subQ2=sQuery(id+"F0.wireOp",EDGE,"E3");Q55=makeQuery(id+"F6.boolean.opBoolean","SPLIT",EDGE,{"disambiguationData":[TD([makeQuery(id+"F4.opPattern","COPY",FACE,{"derivedFrom":makeQuery(id+"F1.opExtrude","SWEPT_FACE",FACE,{"disambiguationData":[OSD([subQ0])]}),"instanceName":"7"})])],"derivedFrom":makeQuery(id+"F6.opExtrude","CAP_EDGE",EDGE,{"disambiguationData":[OSD([subQ2])],"isStart":false})});}
            var Q56;
            {var subQ0=sQuery(id+"F0.wireOp",EDGE,"E9");var subQ1=sQuery(id+"F0.wireOp",EDGE,"E3");Q56=makeQuery(id+"F6.boolean.opBoolean","SPLIT",EDGE,{"disambiguationData":[TD([makeQuery(id+"F4.opPattern","COPY",FACE,{"derivedFrom":makeQuery(id+"F1.opExtrude","SWEPT_FACE",FACE,{"disambiguationData":[OSD([subQ0])]}),"instanceName":"6"})])],"derivedFrom":makeQuery(id+"F6.opExtrude","CAP_EDGE",EDGE,{"disambiguationData":[OSD([subQ1])],"isStart":false})});}
            var Q57;
            {var subQ0=sQuery(id+"F0.wireOp",EDGE,"E9");var subQ2=sQuery(id+"F0.wireOp",EDGE,"E3");Q57=makeQuery(id+"F6.boolean.opBoolean","SPLIT",EDGE,{"disambiguationData":[TD([makeQuery(id+"F4.opPattern","COPY",FACE,{"derivedFrom":makeQuery(id+"F1.opExtrude","SWEPT_FACE",FACE,{"disambiguationData":[OSD([subQ0])]}),"instanceName":"5"})])],"derivedFrom":makeQuery(id+"F6.opExtrude","CAP_EDGE",EDGE,{"disambiguationData":[OSD([subQ2])],"isStart":false})});}
            var Q58;
            {var subQ0=sQuery(id+"F0.wireOp",EDGE,"E9");var subQ2=sQuery(id+"F0.wireOp",EDGE,"E3");Q58=makeQuery(id+"F6.boolean.opBoolean","SPLIT",EDGE,{"disambiguationData":[TD([makeQuery(id+"F4.opPattern","COPY",FACE,{"derivedFrom":makeQuery(id+"F1.opExtrude","SWEPT_FACE",FACE,{"disambiguationData":[OSD([subQ0])]}),"instanceName":"4"})])],"derivedFrom":makeQuery(id+"F6.opExtrude","CAP_EDGE",EDGE,{"disambiguationData":[OSD([subQ2])],"isStart":false})});}
            var Q59;
            {var subQ0=sQuery(id+"F0.wireOp",EDGE,"E9");var subQ2=sQuery(id+"F0.wireOp",EDGE,"E3");Q59=makeQuery(id+"F6.boolean.opBoolean","SPLIT",EDGE,{"disambiguationData":[TD([makeQuery(id+"F4.opPattern","COPY",FACE,{"derivedFrom":makeQuery(id+"F1.opExtrude","SWEPT_FACE",FACE,{"disambiguationData":[OSD([subQ0])]}),"instanceName":"3"})])],"derivedFrom":makeQuery(id+"F6.opExtrude","CAP_EDGE",EDGE,{"disambiguationData":[OSD([subQ2])],"isStart":false})});}
            chamfer(context, id + "F7", {"entities" : qUnion([Q0, Q1, Q2, Q3, Q4, Q5, Q6, Q7, Q8, Q9, Q10, Q11, Q12, Q13, Q14, Q15, Q16, Q17, Q18, Q19, Q20, Q21, Q22, Q23, Q24, Q25, Q26, Q27, Q28, Q29, Q30, Q31, Q32, Q33, Q34, Q35, Q36, Q37, Q38, Q39, Q40, Q41, Q42, Q43, Q44, Q45, Q46, Q47, Q48, Q49, Q50, Q51, Q52, Q53, Q54, Q55, Q56, Q57, Q58, Q59]), "width" : 1 * mm, "tangentPropagation" : true});
        }
    });
